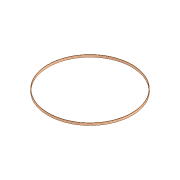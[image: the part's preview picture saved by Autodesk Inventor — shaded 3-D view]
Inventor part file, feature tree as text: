
AUTODESK INVENTOR PART (.ipt)
format: ipt  version: 2021 (Build 250183000, 183)  size: 121,856 bytes
history: native  units: mm
features: extrude x2, sketch x2
ambient origin geometry x8: Origin, YZ Plane, XZ Plane, XY Plane, X Axis, Y Axis, Z Axis, Center Point
bodies: Solid1 (feature_tree), Solid2 (feature_tree)
feature tree (4):
  extrude  "Extrusion1"  TaperAngle=0.0deg  [1 undecoded]
  extrude  "Extrusion2"  [1 undecoded]
  sketch  "Sketch1"  dims[d0=10.0mm d1=0.0mm d2=0.0mm d3=0.0mm]
  sketch  "Sketch2"
note: 2 required parameter values undecoded (feature->parameter linkage not recoverable at this tier; creation-order binding heuristic only, values carry confidence <= 0.55)
